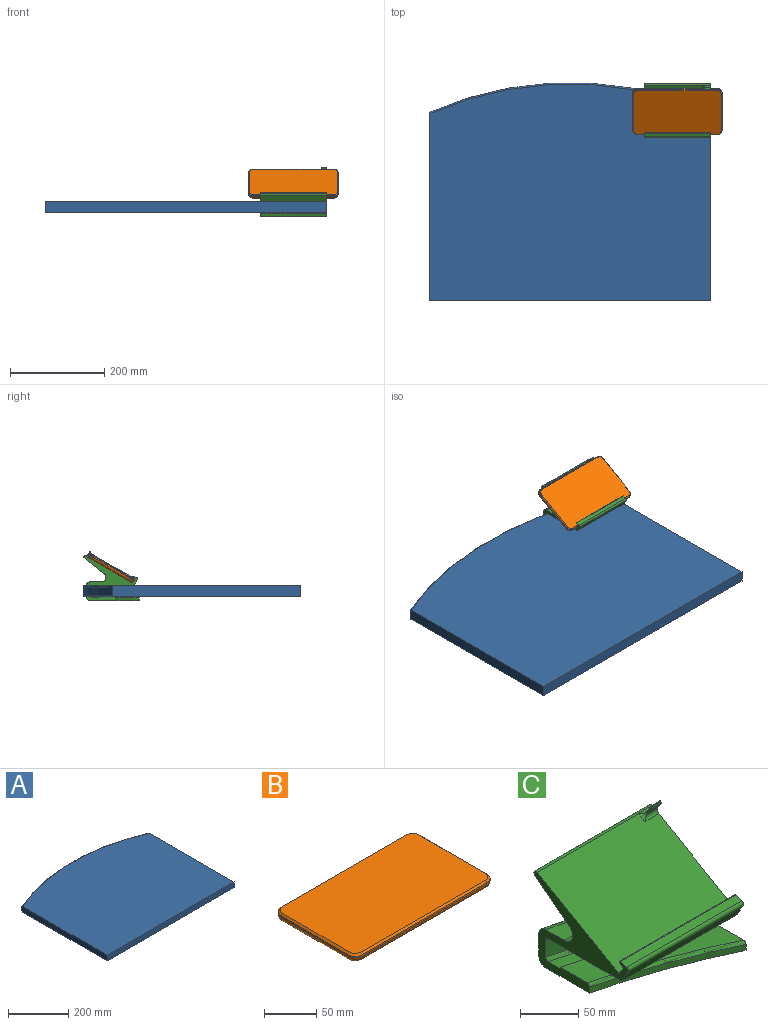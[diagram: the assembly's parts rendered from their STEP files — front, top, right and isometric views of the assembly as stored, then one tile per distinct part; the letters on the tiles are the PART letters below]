
ASSEMBLY  parts=3 mates=1
PART A: 8 faces, bbox 646.6x523.4x23.4 mm
  f0: plane 595x23.4mm, normal (0,-1,0), area 13923mm2, adj f1,f3,f4,f5
  f1: plane 400x23.4mm, normal (1,0,0), area 9355.8mm2, adj f0,f2,f4,f5,f6,f7
  f2: cylinder r=740mm len=595mm, axis (0,0,-1), area 10654.4mm2, adj f1,f3,f6,f7
  f3: plane 400x23.4mm, normal (-1,0,0), area 9355.8mm2, adj f0,f2,f4,f5,f6,f7
  f4: plane 595x459.44mm, normal (0,0,1), area 261145.7mm2, adj f0,f1,f3,f7
  f5: plane 595x459.44mm, normal (0,0,-1), area 261145.7mm2, adj f0,f1,f3,f6
  f6: torus R=737mm, axis (0,0,1), area 2885.8mm2, adj f1,f2,f3,f5
  f7: torus R=737mm, axis (0,0,1), area 2885.7mm2, adj f1,f2,f3,f4
PART B: 26 faces, bbox 189x110.9x10 mm
  f0: plane 169x2mm, normal (0,-1,0), area 338mm2, adj f6,f9,f17,f25
  f1: plane 90.9x2mm, normal (1,0,0), area 181.8mm2, adj f6,f7,f13,f21
  f2: plane 169x2mm, normal (0,1,0), area 338mm2, adj f7,f8,f10,f18
  f3: plane 90.9x2mm, normal (-1,0,0), area 181.8mm2, adj f8,f9,f14,f22
  f4: plane 185x106.9mm, normal (0,0,1), area 19721.6mm2, adj f10,f11,f12,f13,f14,f15,f16,f17
  f5: plane 177x98.9mm, normal (0,0,-1), area 17491.6mm2, adj f18,f19,f20,f21,f22,f23,f24,f25
  f6: cylinder r=10mm len=10mm, axis (0,0,1), area 31.4mm2, adj f0,f1,f15,f23
  f7: cylinder r=10mm len=10mm, axis (0,0,-1), area 31.4mm2, adj f1,f2,f11,f19
  f8: cylinder r=10mm len=10mm, axis (0,0,1), area 31.4mm2, adj f2,f3,f12,f20
  f9: cylinder r=10mm len=10mm, axis (0,0,-1), area 31.4mm2, adj f0,f3,f16,f24
  f10: plane 169x2mm, normal (0,0.71,0.71), area 478mm2, adj f2,f4,f11,f12
  f11: cone r=8mm half-angle=45deg, axis (0,0,-1), area 40mm2, adj f4,f7,f10,f13
  f12: cone r=8mm half-angle=45deg, axis (0,0,-1), area 40mm2, adj f4,f8,f10,f14
  f13: plane 90.9x2mm, normal (0.71,0,0.71), area 257.1mm2, adj f1,f4,f11,f15
  f14: plane 90.9x2mm, normal (-0.71,0,0.71), area 257.1mm2, adj f3,f4,f12,f16
  f15: cone r=8mm half-angle=45deg, axis (0,0,-1), area 40mm2, adj f4,f6,f13,f17
  f16: cone r=8mm half-angle=45deg, axis (0,0,-1), area 40mm2, adj f4,f9,f14,f17
  f17: plane 169x2mm, normal (0,-0.71,0.71), area 478mm2, adj f0,f4,f15,f16
  f18: cylinder r=6mm len=169mm, axis (-1,0,0), area 1592.8mm2, adj f2,f5,f19,f20
  f19: torus R=4mm, axis (0,0,1), area 115.8mm2, adj f5,f7,f18,f21
  f20: torus R=4mm, axis (0,0,1), area 115.8mm2, adj f5,f8,f18,f22
  f21: cylinder r=6mm len=90.9mm, axis (0,1,0), area 856.7mm2, adj f1,f5,f19,f23
  f22: cylinder r=6mm len=90.9mm, axis (0,-1,0), area 856.7mm2, adj f3,f5,f20,f24
  f23: torus R=4mm, axis (0,0,1), area 115.8mm2, adj f5,f6,f21,f25
  f24: torus R=4mm, axis (0,0,1), area 115.8mm2, adj f5,f9,f22,f25
  f25: cylinder r=6mm len=169mm, axis (1,0,0), area 1592.8mm2, adj f0,f5,f23,f24
PART C: 47 faces, bbox 150x119x106.7 mm
  f0: plane 140x98.29mm, normal (0,-0.5,0.87), area 15737.8mm2, adj f10,f11,f25,f35,f41,f43
  f1: plane 140x88.68mm, normal (0,0,-1), area 9544.6mm2, adj f10,f11,f29,f31
  f2: plane 80.91x22.77mm, normal (0,0,1), area 988.8mm2, adj f11,f36,f40
  f3: plane 140.01x47.72mm, normal (0,0.62,-0.79), area 7584.3mm2, adj f10,f11,f34,f36,f37
  f4: plane 140x0.28mm, normal (0,0.87,0.5), area 45.7mm2, adj f10,f11,f34,f35
  f5: plane 140x7.71mm, normal (0,0.87,0.5), area 1246mm2, adj f10,f11,f25,f26
  f6: plane 140x3.46mm, normal (0,0.5,-0.87), area 560mm2, adj f10,f11,f26,f27
  f7: plane 140x0.16mm, normal (0,0.87,0.5), area 25.2mm2, adj f10,f11,f27,f28
  f8: plane 140x7.35mm, normal (0,-0.32,0.95), area 1086.2mm2, adj f10,f11,f28,f33
  f9: plane 140x12.58mm, normal (0,-0.87,-0.5), area 2033.8mm2, adj f10,f11,f29,f33
  f10: plane 119.05x106.7mm, normal (1,0,0), area 2565.1mm2, adj f0,f1,f3,f4,f5,f6,f7,f8
  f11: plane 115.23x96.42mm, normal (-1,0,0), area 2924mm2, adj f0,f1,f2,f3,f4,f5,f6,f7
  f12: cylinder r=740mm len=140mm, axis (0,0,-1), area 3728.7mm2, adj f10,f11,f17,f38,f39,f40
  f13: cylinder r=732mm len=140mm, axis (0,0,1), area 2672mm2, adj f10,f11,f31,f32
  f14: plane 140x61.61mm, normal (0,0,1), area 2070mm2, adj f10,f11,f18,f32
  f15: cylinder r=680mm len=140mm, axis (0,0,1), area 923.6mm2, adj f10,f11,f16,f30
  f16: plane 140x103.39mm, normal (0,0,-1), area 7710.1mm2, adj f10,f11,f15,f17
  f17: torus R=732mm, axis (0,0,-1), area 1856.8mm2, adj f10,f11,f12,f16
  f18: cylinder r=715mm len=140mm, axis (0,0,-1), area 177.6mm2, adj f10,f11,f14,f19
  f19: plane 140x82.63mm, normal (0,0,1), area 4750.3mm2, adj f10,f11,f18,f30
  f20: plane 12.11x7.76mm, normal (0,0.87,0.5), area 107.5mm2, adj f10,f24,f42,f43,f45
  f21: plane 12x0.09mm, normal (0,-0.5,0.87), area 1.3mm2, adj f10,f24,f45,f46
  f22: cylinder r=4mm len=12mm, axis (1,0,0), area 61.9mm2, adj f10,f23,f24,f46
  f23: plane 12.1x3.95mm, normal (0,-0.87,-0.5), area 54.8mm2, adj f10,f22,f24,f41,f43
  f24: plane 8.04x5.28mm, normal (-1,0,0), area 16.1mm2, adj f20,f21,f22,f23,f43,f45,f46
  f25: cylinder r=1mm len=140mm, axis (1,0,0), area 219.9mm2, adj f0,f5,f10,f11
  f26: cylinder r=1mm len=140mm, axis (1,0,0), area 219.9mm2, adj f5,f6,f10,f11
  f27: cylinder r=1mm len=140mm, axis (-1,0,0), area 219.9mm2, adj f6,f7,f10,f11
  f28: cylinder r=1mm len=140mm, axis (1,0,0), area 192.3mm2, adj f7,f8,f10,f11
  f29: cylinder r=1mm len=140mm, axis (-1,0,0), area 146.6mm2, adj f1,f9,f10,f11
  f30: torus R=683mm, axis (0,0,1), area 701.4mm2, adj f10,f11,f15,f19
  f31: torus R=729mm, axis (0,0,1), area 696.2mm2, adj f1,f10,f11,f13
  f32: torus R=729mm, axis (0,0,-1), area 696.2mm2, adj f10,f11,f13,f14
  f33: cylinder r=3mm len=140mm, axis (1,0,0), area 742.6mm2, adj f8,f9,f10,f11
  f34: cylinder r=2.5mm len=140mm, axis (1,0,0), area 500.9mm2, adj f3,f4,f10,f11
  f35: cylinder r=2.5mm len=140mm, axis (1,0,0), area 544.2mm2, adj f0,f4,f10,f11,f42,f44
  f36: cylinder r=10mm len=104.45mm, axis (1,0,0), area 2530.2mm2, adj f2,f3,f11,f37,f39
  f37: bspline ~43.52x32.46mm, area 596.1mm2, adj f3,f10,f36,f38
  f38: bspline ~38.85x15.43mm, area 211.8mm2, adj f10,f12,f37,f39
  f39: bspline ~43.45x17.4mm, area 264.1mm2, adj f12,f36,f38,f40
  f40: torus R=732mm, axis (0,0,-1), area 1075.2mm2, adj f2,f11,f12,f39
  f41: cylinder r=4mm len=17mm, axis (-1,0,0), area 91.4mm2, adj f0,f10,f23,f43
  f42: cylinder r=4mm len=17mm, axis (1,0,0), area 80.1mm2, adj f10,f20,f35,f43,f44
  f43: cylinder r=5mm len=10.25mm, axis (0,0.87,0.5), area 33.6mm2, adj f0,f20,f23,f24,f41,f42,f44
  f44: torus R=7.5mm, axis (1,0,0), area 0.1mm2, adj f35,f42,f43
  f45: cylinder r=0.6mm len=12mm, axis (1,0,0), area 11.3mm2, adj f10,f20,f21,f24
  f46: cylinder r=0.6mm len=12mm, axis (1,0,0), area 5.7mm2, adj f10,f21,f22,f24
PLACE A t=(-85.84,-147.75,7.64)mm
PLACE B rot(axis=(1,0,0),30deg) t=(141.07,56.4,64.16)mm
PLACE C t=(141.66,-3.42,26.79)mm
MATE fastened C.f1 <-> A.f4  axis (0,0,1) through (211.66,52.25,31.04)mm
